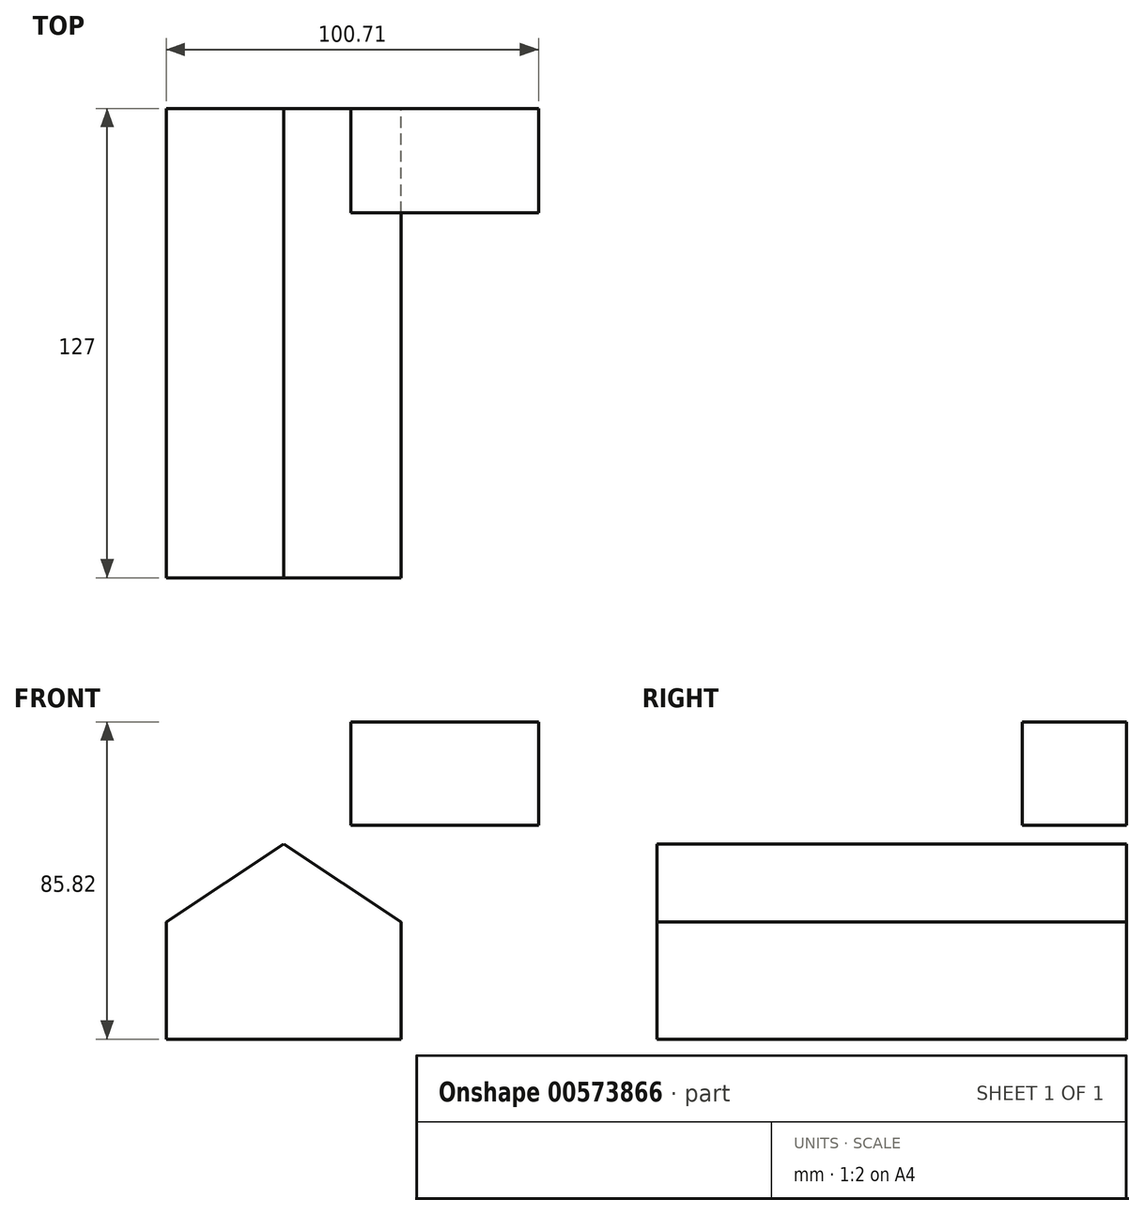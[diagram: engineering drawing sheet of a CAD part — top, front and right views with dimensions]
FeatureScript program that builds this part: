
annotation { "Feature Type Name" : "Feature", "Feature Type Description" : "" }
export const myFeature = defineFeature(function(context is Context, id is Id, definition is map)
    precondition{}
    {
        {
            var Q0;
            Q0=qCreatedBy(makeId("Front.planeOp"),FACE);
            var sketch = newSketch(context, id + "F0", { "sketchPlane" : qUnion([Q0])});
            skLineSegment(sketch, "E0.bottom", {"start": v(44.2, 38.62) * mm, "end": v(-6.6, 38.62) * mm});
            skLineSegment(sketch, "E0.top", {"start": v(44.2, 10.68) * mm, "end": v(-6.6, 10.68) * mm});
            skLineSegment(sketch, "E0.left", {"start": v(44.2, 38.62) * mm, "end": v(44.2, 10.68) * mm});
            skLineSegment(sketch, "E0.right", {"start": v(-6.6, 38.62) * mm, "end": v(-6.6, 10.68) * mm});
            skSolve(sketch);
        }
        {
            var Q0;
            Q0 = qSketchRegion(id + "F0", true);
            extrude(context, id + "F1", {"entities" : qUnion([Q0]), "depth" : 28.2 * mm, "offsetDistance" : 25.4 * mm});
        }
        {
            var Q0;
            Q0=qCreatedBy(makeId("Front.planeOp"),FACE);
            var sketch = newSketch(context, id + "F2", { "sketchPlane" : qUnion([Q0])});
            skLineSegment(sketch, "E1.top", {"start": v(-56.5, -47.2) * mm, "end": v(7, -47.2) * mm});
            skLineSegment(sketch, "E1.left", {"start": v(-56.5, -15.45) * mm, "end": v(-56.5, -47.2) * mm});
            skLineSegment(sketch, "E1.right", {"start": v(7, -15.45) * mm, "end": v(7, -47.2) * mm});
            skLineSegment(sketch, "E2", {"start": v(-56.5, -15.45) * mm, "end": v(-24.75, 5.6) * mm});
            skLineSegment(sketch, "E3", {"start": v(-24.75, 5.6) * mm, "end": v(7, -15.45) * mm});
            skSolve(sketch);
        }
        {
            var Q0;
            Q0 = qSketchRegion(id + "F2", true);
            extrude(context, id + "F3", {"entities" : qUnion([Q0]), "depth" : 127 * mm, "offsetDistance" : 25.4 * mm});
        }
    });
